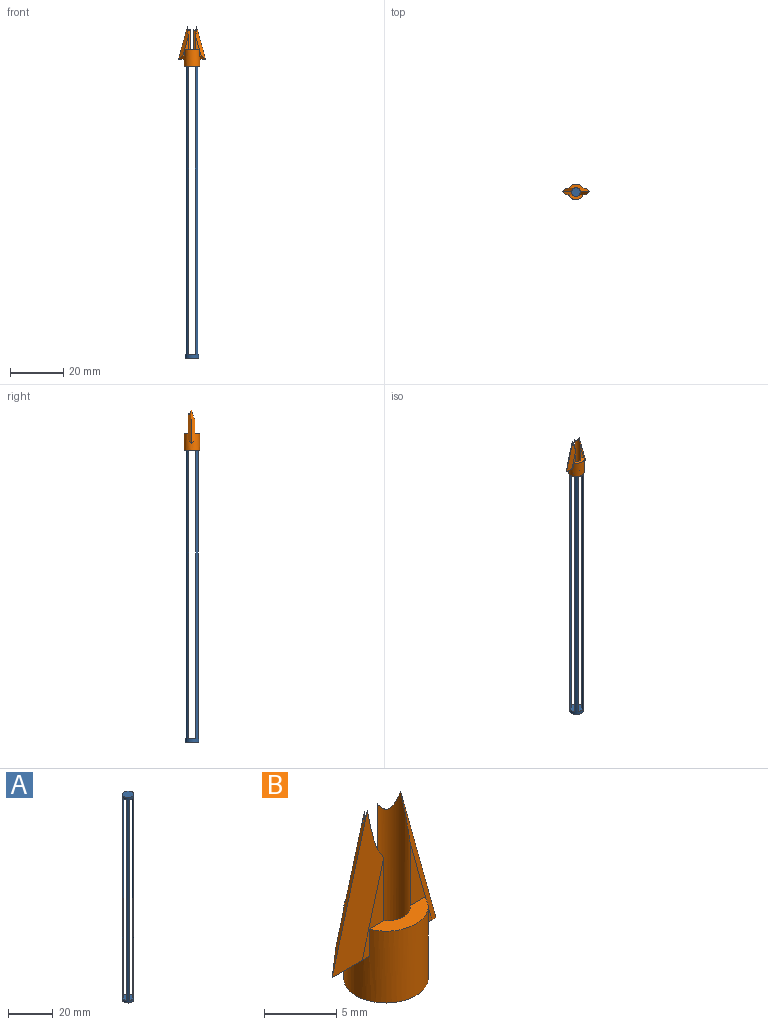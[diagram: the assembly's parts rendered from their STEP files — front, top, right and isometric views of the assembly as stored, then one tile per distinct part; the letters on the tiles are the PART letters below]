
ASSEMBLY  parts=2 mates=1
PART A: 13 faces, bbox 5.1x5.1x112 mm
  f0: plane 109.47x0.93mm, normal (1,0,0), area 101.8mm2, adj f5,f7,f10,f12
  f1: plane 109.47x0.93mm, normal (-1,0,0), area 101.8mm2, adj f5,f7,f8,f12
  f2: plane 5.08x5.08mm, normal (0,0,1), area 20.3mm2, adj f12
  f3: plane 5.08x5.08mm, normal (0,0,-1), area 20.3mm2, adj f12
  f4: plane 109.47x0.93mm, normal (1,0,0), area 101.8mm2, adj f5,f7,f11,f12
  f5: plane 5.08x5.08mm, normal (0,0,1), area 18.2mm2, adj f0,f1,f4,f6,f8,f9,f10,f11
  f6: plane 109.47x0.93mm, normal (-1,0,0), area 101.8mm2, adj f5,f7,f9,f12
  f7: plane 5.08x5.08mm, normal (0,0,-1), area 18.2mm2, adj f0,f1,f4,f6,f8,f9,f10,f11
  f8: plane 109.47x0.93mm, normal (0,-1,0), area 101.8mm2, adj f1,f5,f7,f12
  f9: plane 109.47x0.93mm, normal (0,1,0), area 101.8mm2, adj f5,f6,f7,f12
  f10: plane 109.47x0.93mm, normal (0,-1,0), area 101.8mm2, adj f0,f5,f7,f12
  f11: plane 109.47x0.93mm, normal (0,1,0), area 101.8mm2, adj f4,f5,f7,f12
  f12: cylinder r=2.54mm len=112.01mm, axis (0,0,1), area 622.9mm2, adj f0,f1,f2,f3,f4,f5,f6,f7
PART B: 19 faces, bbox 10.2x5.8x15 mm
  f0: plane 7.68x2.12mm, normal (0,-1,0), area 4.9mm2, adj f5,f10,f13,f14,f18
  f1: plane 7.68x2.12mm, normal (0,-1,0), area 4.9mm2, adj f8,f11,f13,f14,f18
  f2: plane 9.99x2.77mm, normal (0,1,0), area 9.5mm2, adj f7,f9,f12,f13,f18
  f3: plane 9.99x2.77mm, normal (0,1,0), area 9.5mm2, adj f4,f6,f12,f13,f18
  f4: plane 2.55x1.27mm, normal (0,0.71,-0.71), area 2.6mm2, adj f3,f6,f11,f13
  f5: plane 2.37x1.27mm, normal (0,-0.71,-0.71), area 2.5mm2, adj f0,f9,f10,f13
  f6: plane 12.47x4.43mm, normal (0.68,0.71,0.19), area 19.7mm2, adj f3,f4,f8,f18
  f7: plane 12.47x4.43mm, normal (-0.68,0.71,0.19), area 19.7mm2, adj f2,f9,f10,f18
  f8: plane 12.47x3.79mm, normal (0.68,-0.71,0.19), area 18.1mm2, adj f1,f6,f11,f18
  f9: plane 2.55x1.27mm, normal (0,0.71,-0.71), area 2.6mm2, adj f2,f5,f7,f13
  f10: plane 12.47x3.79mm, normal (-0.68,-0.71,0.19), area 18.1mm2, adj f0,f5,f7,f18
  f11: plane 2.37x1.27mm, normal (0,-0.71,-0.71), area 2.5mm2, adj f1,f4,f8,f13
  f12: plane 5.06x1.46mm, normal (0,0,1), area 5.1mm2, adj f2,f3,f13,f18
  f13: cylinder r=2.92mm len=6.1mm, axis (0,0,-1), area 96.5mm2, adj f0,f1,f2,f3,f4,f5,f9,f11
  f14: plane 5.43x1.84mm, normal (0,0,1), area 6.1mm2, adj f0,f1,f13,f18
  f15: plane 5.84x5.84mm, normal (0,0,-1), area 6.5mm2, adj f13,f16
  f16: cylinder r=2.54mm len=5.08mm, axis (0,0,1), area 40.5mm2, adj f15,f17
  f17: plane 5.08x5.08mm, normal (0,0,-1), area 11.8mm2, adj f16,f18
  f18: cylinder r=1.65mm len=12.47mm, axis (0,0,-1), area 80.5mm2, adj f0,f1,f2,f3,f6,f7,f8,f10
PLACE A t=(-14.8,10.19,-9.32)mm
PLACE B t=(-16.84,8.62,27.51)mm
MATE fastened A.f12 <-> B.f18  axis (0,0,1) through (-16.84,7.1,27.51)mm
